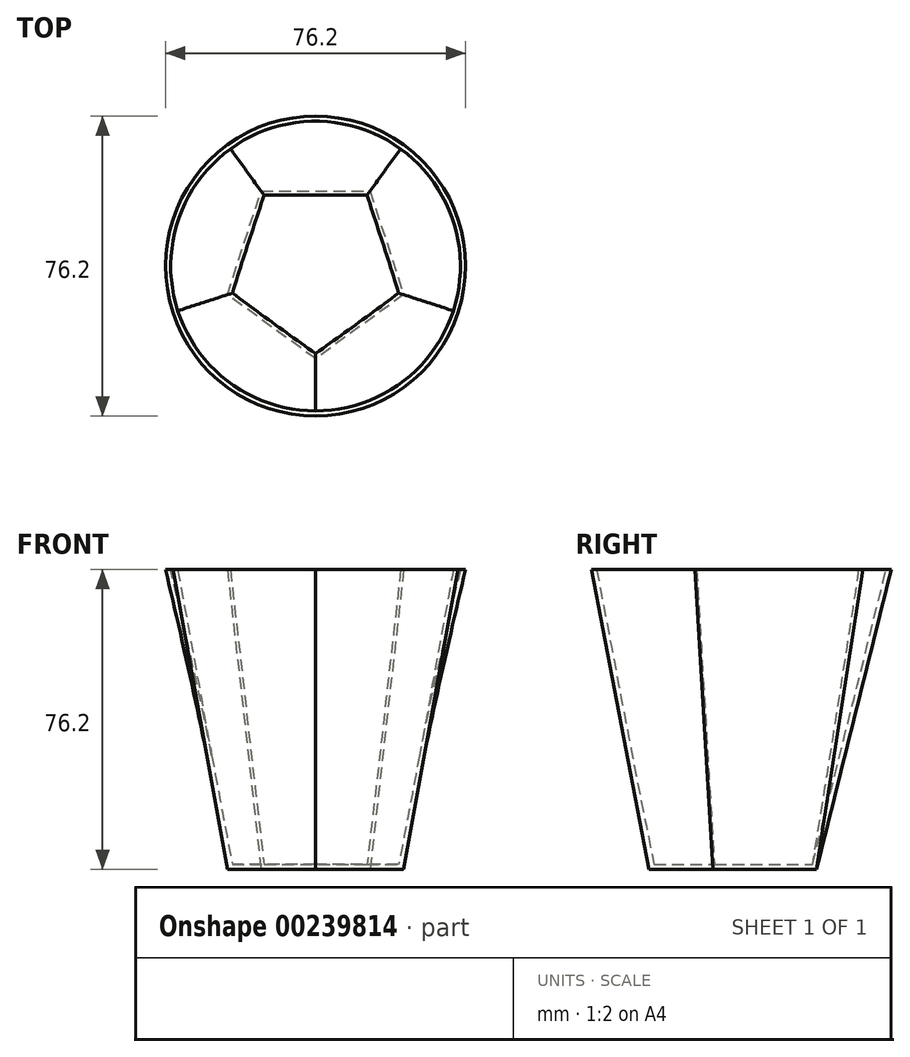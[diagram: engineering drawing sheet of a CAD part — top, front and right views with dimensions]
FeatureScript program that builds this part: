
annotation { "Feature Type Name" : "Feature", "Feature Type Description" : "" }
export const myFeature = defineFeature(function(context is Context, id is Id, definition is map)
    precondition{}
    {
        {
            var Q0;
            Q0=qCreatedBy(makeId("Top.planeOp"),FACE);
            var sketch = newSketch(context, id + "F0", { "sketchPlane" : qUnion([Q0])});
            skCircle(sketch, "E0.cCircle", {"center": v(0, 0) * mm, "radius": 19.05 * mm, "construction": true});
            skLineSegment(sketch, "E0.0", {"start": v(-13.84, 19.05) * mm, "end": v(13.84, 19.05) * mm});
            skLineSegment(sketch, "E0.1", {"start": v(13.84, 19.05) * mm, "end": v(22.4, -7.28) * mm});
            skLineSegment(sketch, "E0.2", {"start": v(22.4, -7.28) * mm, "end": v(0, -23.55) * mm});
            skLineSegment(sketch, "E0.3", {"start": v(0, -23.55) * mm, "end": v(-22.4, -7.28) * mm});
            skLineSegment(sketch, "E0.4", {"start": v(-22.4, -7.28) * mm, "end": v(-13.84, 19.05) * mm});
            skPoint(sketch, "E0.0.midPoint", {"position": v(0, 19.05) * mm});
            skSolve(sketch);
        }
        {
            var Q0;
            Q0=qCreatedBy(makeId("Top.planeOp"),FACE);
            cPlane(context, id + "F1", {"entities" : qUnion([Q0]), "cplaneType" : CPlaneType.OFFSET, "offset" : 76.2 * mm, "width" : 152.4 * mm, "height" : 152.4 * mm});
        }
        {
            var Q0;
            Q0=qCreatedBy(id+"F1.planeOp",FACE);
            var sketch = newSketch(context, id + "F2", { "sketchPlane" : qUnion([Q0])});
            skCircle(sketch, "E1", {"center": v(0, 0) * mm, "radius": 38.1 * mm});
            skSolve(sketch);
        }
        {
            var Q0;
            Q0=makeQuery(id+"F2.imprint","IMPRINT",FACE,{"disambiguationData":[TD([[makeQuery(id+"F2.imprint","IMPRINT",EDGE,{"derivedFrom":sQuery(id+"F2.wireOp",EDGE,"E1")}),1.0]])]});
            var Q1;
            Q1=makeQuery(id+"F0.imprint","IMPRINT",FACE,{"disambiguationData":[TD([[makeQuery(id+"F0.imprint","IMPRINT",EDGE,{"derivedFrom":sQuery(id+"F0.wireOp",EDGE,"E0.0")}),-1.0]])]});
            loft(context, id + "F3", {"sheetProfilesArray" : [{ "sheetProfileEntities" : qUnion([Q0]) }, { "sheetProfileEntities" : qUnion([Q1]) }]});
        }
        {
            var Q0;
            Q0=makeQuery(id+"F3.opLoft","CAP_FACE",FACE,{"disambiguationData":[OSD([makeQuery(id+"F2.imprint","IMPRINT",FACE,{"disambiguationData":[TD([[makeQuery(id+"F2.imprint","IMPRINT",EDGE,{"derivedFrom":sQuery(id+"F2.wireOp",EDGE,"E1")}),1.0]])]})])],"isStart":true});
            shell(context, id + "F4", {"entities" : qUnion([Q0]), "thickness" : 1.27 * mm});
        }
    });
